# Revit family: BL-SH-3012-R60BC-IC-I
name_source: partatom
category: Furniture
units: mm (PartAtom-declared; Revit-internal decimal feet)

## family parameters
Always vertical = Yes
Cut with Voids When Loaded = No
OmniClass Number = 23.40.20.00
OmniClass Title = General Furniture and Specialties
Room Calculation Point = No
Shared = No
Work Plane-Based = No

## types (32) — shared parameters
D = 20"
Default Elevation = 0"
HA 30 = No
NUMBER PB = 2
Width = 36"
zero-valued in all types: ES Book Volume Ct, MS-HS Book Volume Ct

## per-type parameters (varying)
| type | Adder | End | HA 36 | HA 42 | HA 48 | HA 60 | HA 72 | HA 82 | Height | Island | Model | Picture book | Starter |
| BL-SH-3012-R60BC-IC-S-HA42 | No | No | No | Yes | No | No | No | No | 42" | No | BL-SH-3012-R60BC-IC-S-HA42 | No | Yes |
| BL-SH-3012-R60PB-IC-S-HA42 | No | No | No | Yes | No | No | No | No | 42" | No | BL-SH-3012-R60PB-IC-S-HA42 | Yes | Yes |
| BL-SH-3012-R60PB-IC-A-HA42 | No | No | No | Yes | No | No | No | No | 42" | No | BL-SH-3012-R60BC-IC-A-HA42 | Yes | No |
| BL-SH-3012-R60BC-IC-A-HA42 | No | No | No | Yes | No | No | No | No | 42" | No | BL-SH-3012-R60BC-IC-A-HA42 | No | No |
| BL-SH-3012-R60BC-IC-E | No | Yes | No | No | No | No | No | No | 42" | No | BL-SH-3012-R60BC-IC-E | No | No |
| BL-SH-3012-R60BC-IC-A | Yes | No | No | No | No | No | No | No | 42" | No | BL-SH-3012-R60BC-IC-A | No | No |
| BL-SH-3012-R60BC-IC-S | Yes | No | No | No | No | No | No | No | 42" | No | BL-SH-3012-R60BC-IC-S | No | Yes |
| BL-SH-3012-R60BC-IC-I | No | No | No | No | No | No | No | No | 42" | Yes | BL-SH-3012-R60BC-IC-I | No | No |
| BL-SH-3012-R60BC-IC-S-HA82 | No | No | No | No | No | No | No | Yes | 42" | No | BL-SH-3012-R60BC-IC-S-HA82 | No | Yes |
| BL-SH-3012-R60BC-IC-S-HA72 | No | No | No | No | No | No | Yes | No | 42" | No | BL-SH-3012-R60BC-IC-S-HA72 | No | Yes |
| BL-SH-3012-R60BC-IC-S-HA60 | No | No | No | No | No | Yes | No | No | 42" | No | BL-SH-3012-R60BC-IC-S-HA60 | No | Yes |
| BL-SH-3012-R60BC-IC-S-HA48 | No | No | No | No | Yes | No | No | No | 42" | No | BL-SH-3012-R60BC-IC-S-HA48 | No | Yes |
| BL-SH-3012-R60BC-IC-A-HA72 | No | No | No | No | No | No | Yes | No | 42" | No | BL-SH-3012-R60BC-IC-A-HA72 | No | No |
| BL-SH-3012-R60BC-IC-A-HA48 | No | No | No | No | Yes | No | No | No | 42" | No | BL-SH-3012-R60BC-IC-A-HA48 | No | No |
| BL-SH-3012-R60BC-IC-A-HA60 | No | No | No | No | No | Yes | No | No | 42" | No | BL-SH-3012-R60BC-IC-A-HA60 | No | No |
| BL-SH-3012-R60BC-IC-A-HA82 | No | No | No | No | No | No | No | Yes | 42" | No | BL-SH-3012-R60BC-IC-A-HA82 | No | No |
| BL-SH-3012-R60BC-IC-A-HA36 | No | No | Yes | No | No | No | No | No | 42" | No | BL-SH-3012-R60BC-IC-A-HA36 | No | No |
| BL-SH-3012-R60PB-IC-A | Yes | No | No | No | No | No | No | No | 42" | No | BL-SH-3012-R60PB-IC-A | Yes | No |
| BL-SH-3012-R60PB-IC-S-HA36 | No | No | Yes | No | No | No | No | No | 42" | No | BL-SH-3012-R60PB-IC-S-HA36 | Yes | Yes |
| BL-SH-3012-R60BC-IC-S-HA36 | No | No | Yes | No | No | No | No | No | 42" | No | BL-SH-3012-R60BC-IC-S-HA36 | No | Yes |
| BL-SH-3012-R60PB-IC-S-HA82 | No | No | No | No | No | No | No | Yes | 42" | No | BL-SH-3012-R60PB-IC-S-HA82 | Yes | Yes |
| BL-SH-3012-R60PB-IC-S-HA72 | No | No | No | No | No | No | Yes | No | 42" | No | BL-SH-3012-R60PB-IC-S-HA72 | Yes | Yes |
| BL-SH-3012-R60PB-IC-S-HA60 | No | No | No | No | No | Yes | No | No | 42" | No | BL-SH-3012-R60PB-IC-S-HA60 | Yes | Yes |
| BL-SH-3012-R60PB-IC-S-HA48 | No | No | No | No | Yes | No | No | No | 42" | No | BL-SH-3012-R60PB-IC-S-HA48 | Yes | Yes |
| BL-SH-3012-R60PB-IC-S | Yes | No | No | No | No | No | No | No | 42" | No | BL-SH-3012-R60PB-IC-S | Yes | Yes |
| BL-SH-3012-R60PB-IC-I | No | No | No | No | No | No | No | No | 42" | Yes | BL-SH-3012-R60PB-IC-I | Yes | No |
| BL-SH-3012-R60PB-IC-E | No | Yes | No | No | No | No | No | No | 42" | No | BL-SH-3012-R60PB-IC-E | Yes | No |
| BL-SH-3012-R60PB-IC-A-HA82 | No | No | No | No | No | No | No | Yes | 30" | No | BL-SH-3012-R60PB-IC-A-HA82 | Yes | No |
| BL-SH-3012-R60PB-IC-A-HA72 | No | No | No | No | No | No | Yes | No | 42" | No | BL-SH-3012-R60PB-IC-A-HA72 | Yes | No |
| BL-SH-3012-R60PB-IC-A-HA60 | No | No | No | No | No | Yes | No | No | 42" | No | BL-SH-3012-R60PB-IC-A-HA60 | Yes | No |
| BL-SH-3012-R60PB-IC-A-HA48 | No | No | No | No | Yes | No | No | No | 42" | No | BL-SH-3012-R60PB-IC-A-HA48 | Yes | No |
| BL-SH-3012-R60PB-IC-A-HA36 | No | No | Yes | No | No | No | No | No | 30" | No | BL-SH-3012-R60PB-IC-A-HA36 | Yes | No |

## geometry (parser evidence)
native form markers: Sweep x29
no freeform markers — native parametric forms only
